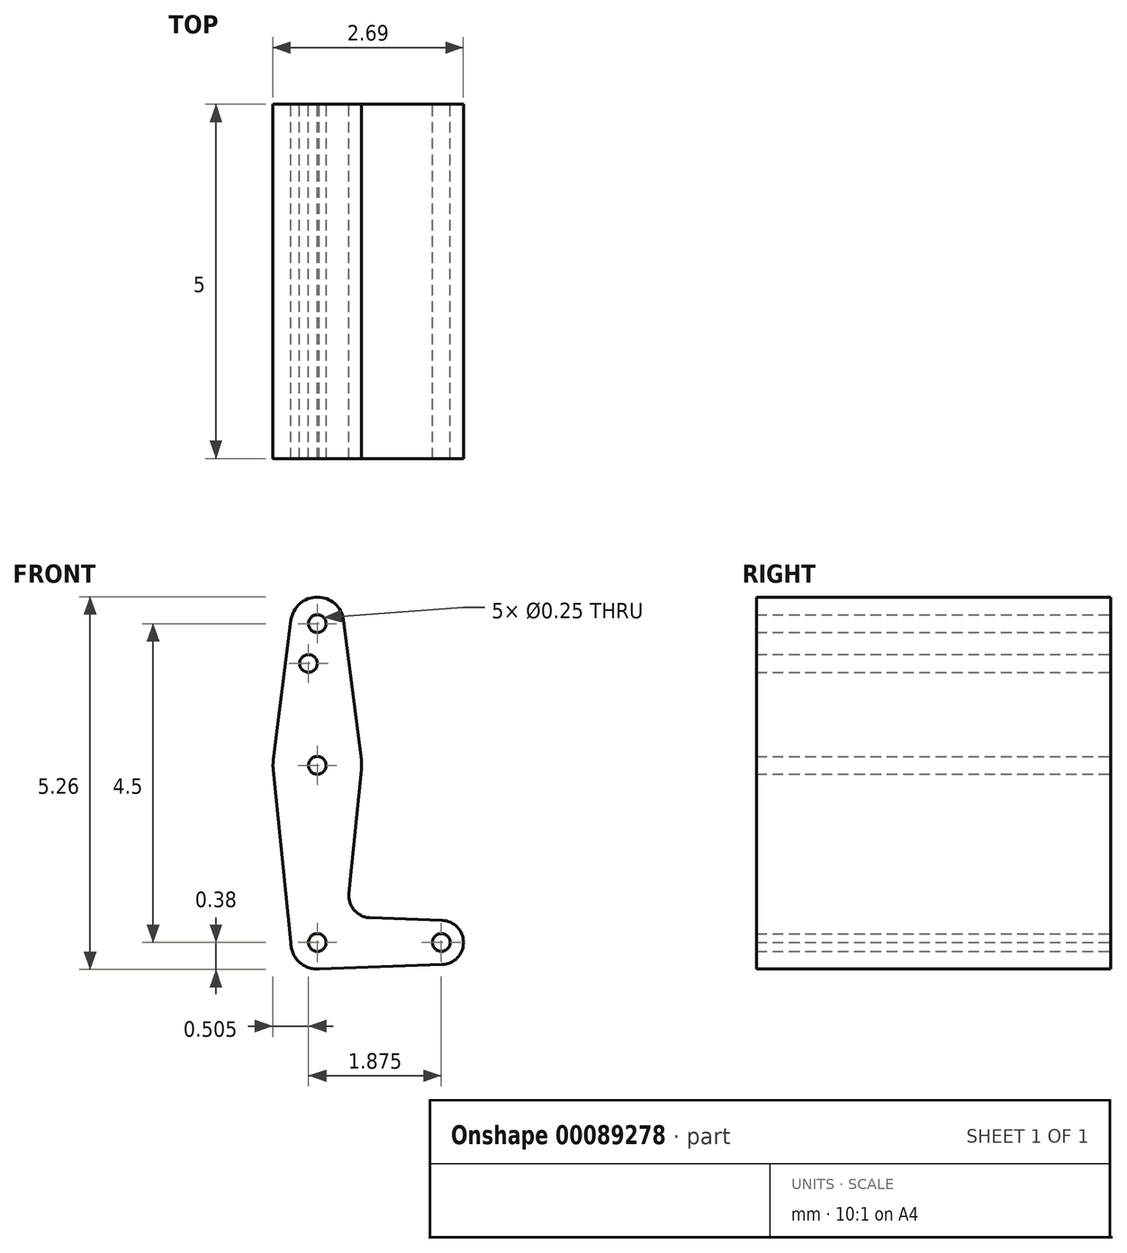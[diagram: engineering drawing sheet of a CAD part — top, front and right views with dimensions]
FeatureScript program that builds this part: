
annotation { "Feature Type Name" : "Feature", "Feature Type Description" : "" }
export const myFeature = defineFeature(function(context is Context, id is Id, definition is map)
    precondition{}
    {
        {
            var Q0;
            Q0=qCreatedBy(makeId("Front.planeOp"),FACE);
            var sketch = newSketch(context, id + "F0", { "sketchPlane" : qUnion([Q0])});
            skLineSegment(sketch, "E0", {"start": v(0, 0) * mm, "end": v(0, 4.5) * mm, "construction": true});
            skLineSegment(sketch, "E1", {"start": v(0, 0) * mm, "end": v(1.75, 0) * mm, "construction": true});
            skCircle(sketch, "E2", {"center": v(1.75, 0) * mm, "radius": 0.31 * mm});
            skCircle(sketch, "E3", {"center": v(0, 4.5) * mm, "radius": 0.37 * mm});
            skCircle(sketch, "E4", {"center": v(0, 2.5) * mm, "radius": 0.62 * mm});
            skCircle(sketch, "E5", {"center": v(0, 0) * mm, "radius": 0.38 * mm});
            skLineSegment(sketch, "E6", {"start": v(-0.37, 0) * mm, "end": v(-0.62, 2.44) * mm});
            skLineSegment(sketch, "E7", {"start": v(0, -0.38) * mm, "end": v(1.76, -0.31) * mm});
            skLineSegment(sketch, "E8", {"start": v(0.62, 2.58) * mm, "end": v(0.37, 4.55) * mm});
            skCircle(sketch, "E9", {"center": v(0, 0) * mm, "radius": 0.12 * mm});
            skCircle(sketch, "E10", {"center": v(1.75, 0) * mm, "radius": 0.12 * mm});
            skCircle(sketch, "E11", {"center": v(0, 2.5) * mm, "radius": 0.12 * mm});
            skCircle(sketch, "E12", {"center": v(-0.12, 3.94) * mm, "radius": 0.12 * mm});
            skLineSegment(sketch, "E13", {"start": v(-0.37, 4.55) * mm, "end": v(-0.62, 2.58) * mm});
            skCircle(sketch, "E14", {"center": v(0, 4.5) * mm, "radius": 0.12 * mm});
            skLineSegment(sketch, "E15", {"start": v(0.62, 2.44) * mm, "end": v(0.45, 0.7) * mm});
            skLineSegment(sketch, "E16", {"start": v(1.76, 0.31) * mm, "end": v(0.75, 0.35) * mm});
            skArc(sketch, "E17.filletArc", {"start": v(0.45, 0.7) * mm, "mid": v(0.52, 0.46) * mm, "end": v(0.75, 0.35) * mm});
            skSolve(sketch);
        }
        {
            var Q0;
            Q0 = qSketchRegion(id + "F0", true);
            extrude(context, id + "F1", {"entities" : qUnion([Q0]), "depth" : 5 * mm});
        }
    });
